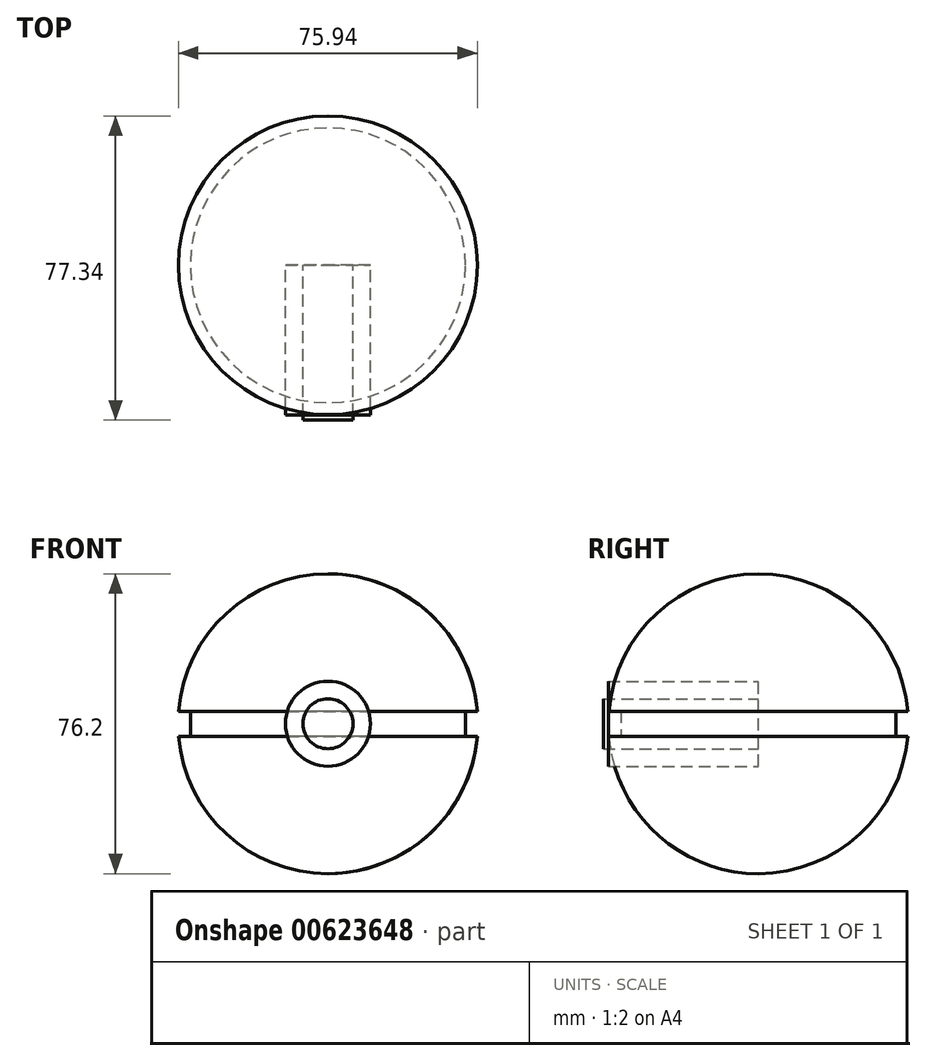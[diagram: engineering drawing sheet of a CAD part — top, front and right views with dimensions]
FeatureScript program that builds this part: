
annotation { "Feature Type Name" : "Feature", "Feature Type Description" : "" }
export const myFeature = defineFeature(function(context is Context, id is Id, definition is map)
    precondition{}
    {
        {
            var Q0;
            Q0=qCreatedBy(makeId("Top.planeOp"),FACE);
            var sketch = newSketch(context, id + "F0", { "sketchPlane" : qUnion([Q0])});
            skCircle(sketch, "E0", {"center": v(0, 0) * mm, "radius": 38.1 * mm});
            skSolve(sketch);
        }
        {
            var Q0;
            Q0 = qSketchRegion(id + "F0", true);
            extrude(context, id + "F1", {"entities" : qUnion([Q0]), "endBound" : BoundingType.SYMMETRIC, "depth" : 76.2 * mm, "offsetDistance" : 25.4 * mm});
        }
        {
            var Q0;
            Q0=makeQuery(id+"F1.opExtrude","CAP_EDGE",EDGE,{"disambiguationData":[OSD([sQuery(id+"F0.wireOp",EDGE,"E0")])],"isStart":false});
            var Q1;
            Q1=makeQuery(id+"F1.opExtrude","CAP_EDGE",EDGE,{"disambiguationData":[OSD([sQuery(id+"F0.wireOp",EDGE,"E0")])],"isStart":true});
            fillet(context, id + "F2", {"entities" : qUnion([Q0, Q1]), "radius" : 38.1 * mm, "tangentPropagation" : true, "allowEdgeOverflow" : false});
        }
        {
            var Q0;
            Q0=qCreatedBy(makeId("Top.planeOp"),FACE);
            var sketch = newSketch(context, id + "F3", { "sketchPlane" : qUnion([Q0])});
            skCircle(sketch, "E1", {"center": v(0, 0) * mm, "radius": 38.1 * mm});
            skSolve(sketch);
        }
        {
            var Q0;
            Q0 = qSketchRegion(id + "F3", true);
            extrude(context, id + "F4", {"entities" : qUnion([Q0]), "operationType" : NewBodyOperationType.REMOVE, "endBound" : BoundingType.SYMMETRIC, "oppositeDirection" : true, "depth" : 6.35 * mm, "offsetDistance" : 25.4 * mm});
        }
        {
            var Q0;
            Q0=qCreatedBy(makeId("Top.planeOp"),FACE);
            var sketch = newSketch(context, id + "F5", { "sketchPlane" : qUnion([Q0])});
            skCircle(sketch, "E2", {"center": v(0, 0) * mm, "radius": 34.93 * mm});
            skSolve(sketch);
        }
        {
            var Q0;
            Q0 = qSketchRegion(id + "F5", true);
            extrude(context, id + "F6", {"entities" : qUnion([Q0]), "endBound" : BoundingType.SYMMETRIC, "depth" : 6.35 * mm, "offsetDistance" : 25.4 * mm});
        }
        {
            var Q0;
            Q0=qCreatedBy(makeId("Front.planeOp"),FACE);
            var sketch = newSketch(context, id + "F7", { "sketchPlane" : qUnion([Q0])});
            skCircle(sketch, "E3", {"center": v(0, 0) * mm, "radius": 10.8 * mm});
            skSolve(sketch);
        }
        {
            var Q0;
            Q0 = qSketchRegion(id + "F7", true);
            extrude(context, id + "F8", {"entities" : qUnion([Q0]), "depth" : 38.1 * mm, "offsetDistance" : 25.4 * mm});
        }
        {
            var Q0;
            Q0=qCreatedBy(makeId("Front.planeOp"),FACE);
            var sketch = newSketch(context, id + "F9", { "sketchPlane" : qUnion([Q0])});
            skCircle(sketch, "E4", {"center": v(0, 0) * mm, "radius": 6.35 * mm});
            skSolve(sketch);
        }
        {
            var Q0;
            Q0 = qSketchRegion(id + "F9", true);
            extrude(context, id + "F10", {"entities" : qUnion([Q0]), "depth" : 39.37 * mm, "offsetDistance" : 25.4 * mm});
        }
    });
